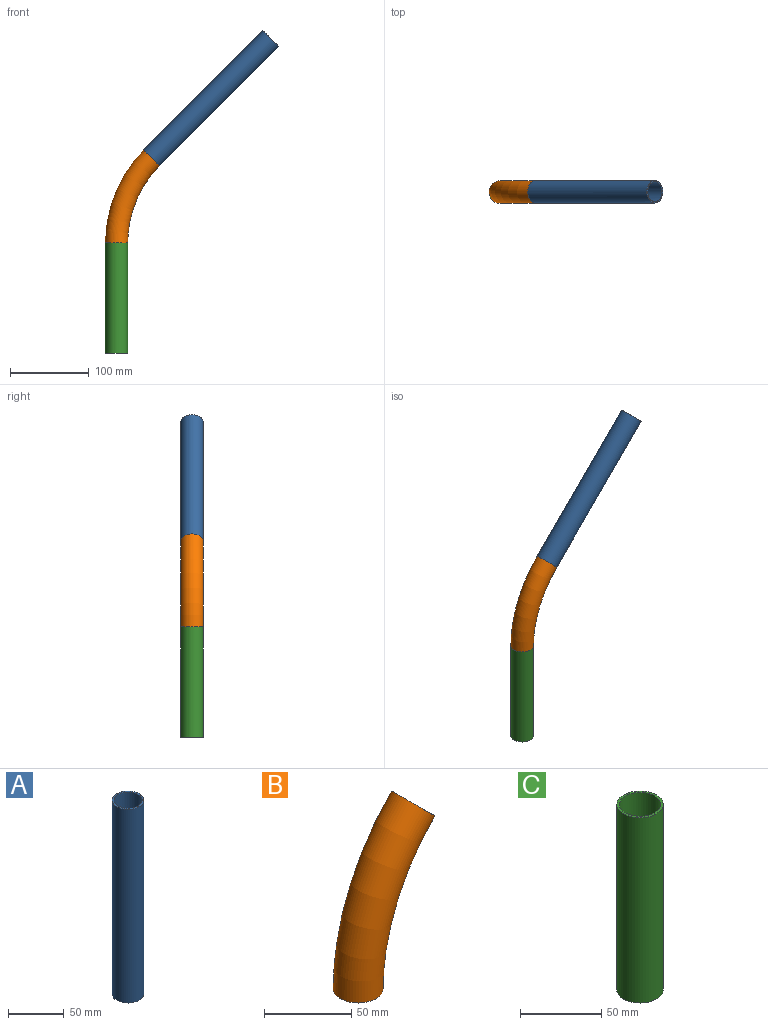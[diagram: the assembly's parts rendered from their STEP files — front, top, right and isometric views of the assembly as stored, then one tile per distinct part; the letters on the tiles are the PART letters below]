
ASSEMBLY  parts=3 mates=2
PART A: 4 faces, bbox 28.6x28.6x213.4 mm
  f0: cylinder r=12.7mm len=213.36mm, axis (0,0,-1), area 17025.4mm2, adj f2,f3
  f1: cylinder r=14.29mm len=213.36mm, axis (0,0,-1), area 19153.5mm2, adj f2,f3
  f2: plane 28.58x28.58mm, normal (0,0,1), area 134.6mm2, adj f0,f1
  f3: plane 28.58x28.58mm, normal (0,0,-1), area 134.6mm2, adj f0,f1
PART B: 3 faces, bbox 82.8x28.6x127.6 mm
  f0: torus R=152.4mm, axis (0,-1,0), area 10745.1mm2, adj f1,f2
  f1: plane 28.58x20.21mm, normal (0.71,0,0.71), area 641.3mm2, adj f0
  f2: plane 28.58x28.58mm, normal (0,0,-1), area 641.3mm2, adj f0
PART C: 4 faces, bbox 28.6x28.6x139.7 mm
  f0: cylinder r=12.7mm len=139.7mm, axis (0,0,-1), area 11147.6mm2, adj f2,f3
  f1: cylinder r=14.29mm len=139.7mm, axis (0,0,-1), area 12541mm2, adj f2,f3
  f2: plane 28.58x28.58mm, normal (0,0,1), area 134.6mm2, adj f0,f1
  f3: plane 28.58x28.58mm, normal (0,0,-1), area 134.6mm2, adj f0,f1
PLACE A rot(axis=(0,1,0),45deg) t=(44.64,0,171.26)mm
PLACE B t=(152.4,0,63.5)mm
PLACE C t=(0,0,-76.2)mm
MATE fastened B.f2 <-> C.f0  axis (0,0,-1) through (0,0,63.5)mm
MATE fastened A.f0 <-> B.f1  axis (-0.71,0,-0.71) through (44.64,0,171.26)mm
